# Revit family: PRD_AR_MxrTps_ThermostaticSingle-leverPillarMixer_F5LT1001-F5LT1003
name_source: partatom
category: Plumbing Fixtures
units: mm (PartAtom-declared; Revit-internal decimal feet)

## family parameters
Always vertical = Yes
Cut with Voids When Loaded = No
OmniClass Number = 23.45.55.17
OmniClass Title = Mixing Faucets
Part Type = Normal
Room Calculation Point = No
Round Connector Dimension = Use Diameter
Shared = No
Work Plane-Based = No

## types (3) — shared parameters
AccentColour = none
AssetType = Fixed
BasicColour = chrome-look (glossy)
BodyMaterial = PRD_AR_ChromatedBrass_HighPolished
Category = Pr_40_20_87_55, Mixer taps
CloseOffRating = 0.0 Pa
Color = chrome-look (glossy)
Depressurised = no
DiameterNominal = 15 mm
DurationUnit = year
FaucetFunction = Mixed
FaucetOperation = LeverHandle
FaucetType = Pillar
Finish = polished chrome-plated
FunctionalPrinciple = manual
IfcExportAs = IfcValveType
IfcExportType = FAUCET
InletSize = G 3/8
LockingMechanism = Top section, ceramic
Manufacturer = KWC Group AG
ManufacturerName = KWC Group AG
ManufacturerURL = www.kwc.com
Material = Brass
MaterialFitting = brass-look
MinimumFlowPressure = 1 bar
NBSDescription = Taps and water supply fittings for sinks
NBSReference = 45-35-70/345
NominalWidth = 50 mm  [stored 0.164042 ft]
ProductInformation = http://pim.kwc.com
Shape = Pillar tap
Size = 15
SoundInsulation = no
Spout = fixed
Status = New
SurfaceFinishFitting = chromed
SurfaceTreatmentFitting = polished
TailorMade = no
TemperatureLimit = yes
TestPressure = 0.0 Pa
TypeOfMixing = with thermostat
TypeOfMounting = tap hole
TypeOfOperation = manual operation
TypeOfTap = pillar tap
URL = www.kwc.com
Uniclass2015Code = Pr_40_20_87_55
Uniclass2015Title = Mixer taps
Uniclass2015Version = Products v1.32
ValveMechanism = OTHER
ValveOperation = LEVER
ValvePattern = STRAIGHT_3_PORT
Version = 1
VolumeFlowRate = 0.08 l/s at 3 bar
WarrantyDurationUnit = year
WaterConnection = hose (gland nut)
WithBackflowPreventer = no
WithFilter = yes
WithRosettesOrCoverPlate = no
WorkingPressure = 0.0 Pa
zero-valued in all types: Default Elevation, FlowCoefficient, NominalDepth

## per-type parameters (varying)
| type | BIMObjectName | Description | Features | Height | HygieneFlushing | IntegralAccessories | Length | ModelNumber | Name | NominalHeight | Pop-upWasteSet | Pop-upWasteSetTurnOn | SpoutProjection | ThermalDisinfection |
| F5LT1001 | PRD_AR_MixerTaps_ThermostaticSingle-leverPillarMixer_F5LT1001 | F5L-Therm thermostatic single-lever mixer as DN 15 pillar mixer for sanitary facilities. Thermostatically-controlled mixer cartridge with expansion element and active scald protection as well as adjustable and turn-proof temperature stop, and ceramic disc technology. With mechanism for optional hygiene unit for automatic hygiene flushing, program-controlled thermal disinfection and storage of statistical data. For connection to hot water and cold water via hoses, includes strainers. All-metal construction, high-polished chrome-plated brass. Anti-theft aerator, slim design, with integrated flow rate controller 5.0 l/min, projection 100 mm. | For connection to hot water and cold water via hoses, includes strainers. With integrated flow rate controller 5.0 l/min, projection 100 mm. | 135 mm  [stored 0.442913 ft] | prepared |  | 100 mm  [stored 0.328084 ft] | 2030066480 | F5L-Therm thermostatic single-lever pillar mixer F5LT1001 | 135 mm  [stored 0.442913 ft] | no | No | 100 mm | yes |
| F5LT1002 | PRD_AR_MixerTaps_ThermostaticSingle-leverPillarMixer_F5LT1002 | F5L-Therm thermostatic single-lever mixer as DN 15 pillar mixer for sanitary facilities. Thermostatically-controlled mixer cartridge with expansion element and active scald protection as well as adjustable and turn-proof temperature stop, and ceramic disc technology. With mechanism for optional hygiene unit for automatic hygiene flushing, program-controlled thermal disinfection and storage of statistical data. For connection to hot water and cold water via hoses, includes strainers. All-metal construction, highpolished chrome-plated brass. Anti-theft aerator, SLIM design, with integrated flow rate controller 5.0 l/min, projection 125 mm. | For connection to hot water and cold water via hoses, includes strainers. With integrated flow rate controller 5.0 l/min, projection 125 mm. | 160 mm  [stored 0.524934 ft] | prepared |  | 125 mm  [stored 0.410105 ft] | 2030066481 | F5L-Therm thermostatic single-lever pillar mixer F5LT1002 | 160 mm  [stored 0.524934 ft] | no | No | 125 mm | yes |
| F5LT1003 | PRD_AR_MixerTaps_ThermostaticSingle-leverPillarMixer_F5LT1003 | F5L-Therm thermostatic single-lever mixer as DN 15 pillar mixer for sanitary facilities. Thermostatically-controlled mixer cartridge with expansion element and active scald protection as well as adjustable and turn-proof temperature stop, and ceramic disc technology. For connection to hot water and cold water via hoses, includes strainers. All-metal construction, high-polished chrome-plated brass. Anti-theft aerator, SLIM design, with integrated flow rate controller 5.0 l/min, projection 125 mm. With pop-up waste set drain fitting G 1 1/4 mm, chrome-plated. | For connection to hot water and cold water via hoses, includes strainers. With integrated flow rate controller 5.0 l/min, projection 125 mm. | 160 mm  [stored 0.524934 ft] | no | pop-up waste set drain fitting G 1 1/4 | 125 mm  [stored 0.410105 ft] | 2030066482 | F5L-Therm thermostatic single-lever pillar mixer with pop-up waste set F5LT1003 | 160 mm  [stored 0.524934 ft] | yes | Yes | 125 mm | no |

note: column(s) folded — value = type name in every type: Model, ModelReference

note: [stored X ft] marks values corroborated as IEEE doubles in the binary element streams (Revit-internal decimal feet)

## geometry (parser evidence)
native form markers: Sweep x17
no freeform markers — native parametric forms only
